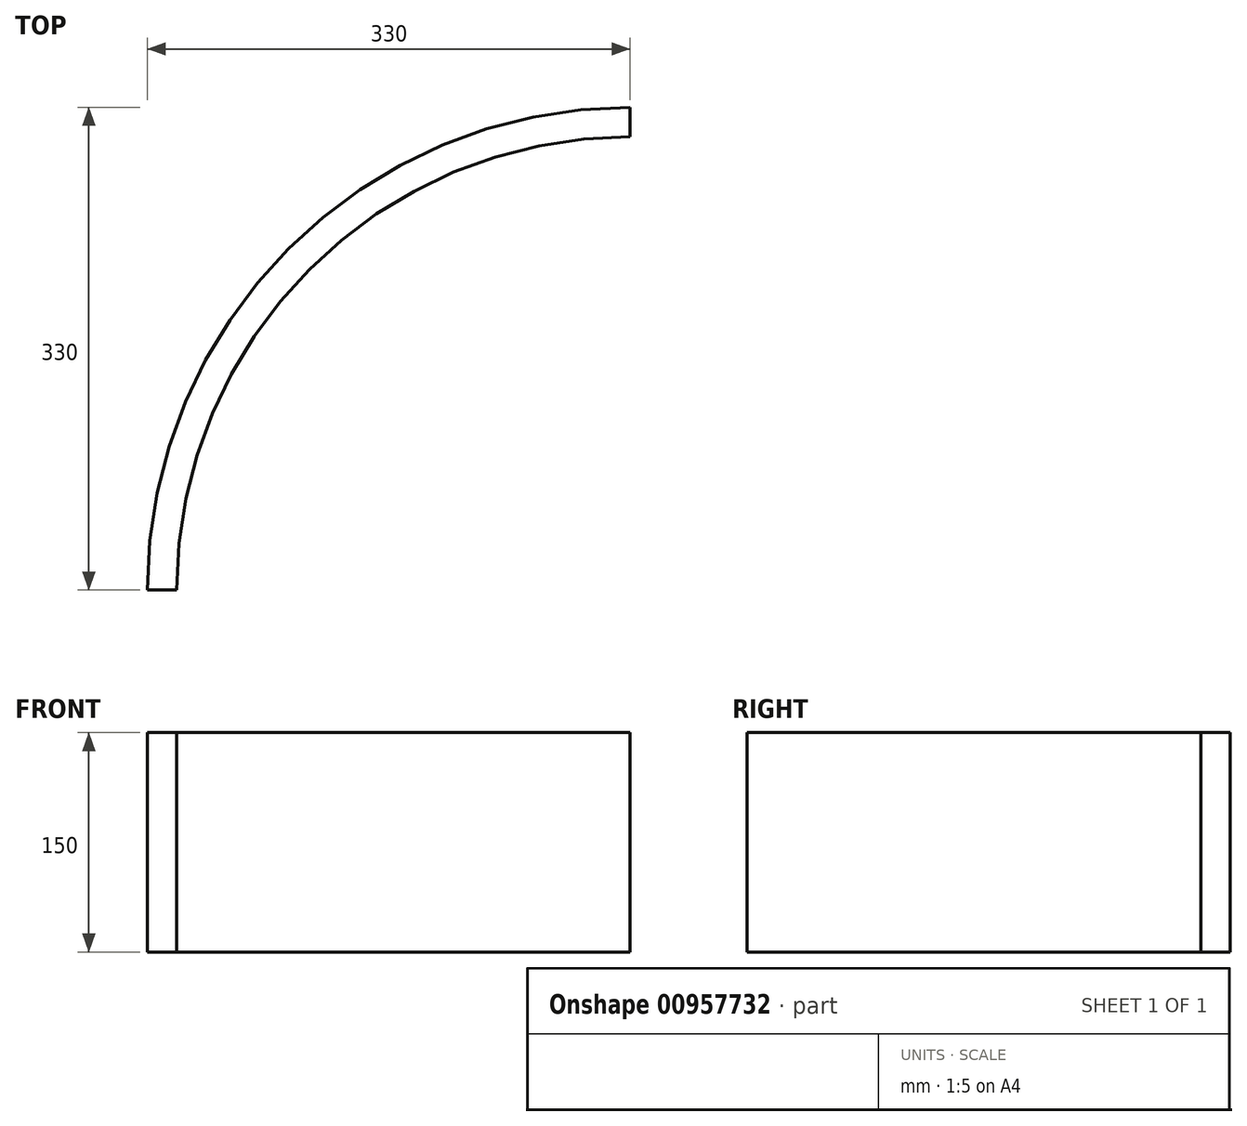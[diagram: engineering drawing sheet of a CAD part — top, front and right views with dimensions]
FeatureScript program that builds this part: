
annotation { "Feature Type Name" : "Feature", "Feature Type Description" : "" }
export const myFeature = defineFeature(function(context is Context, id is Id, definition is map)
    precondition{}
    {
        {
            var Q0;
            Q0=qCreatedBy(makeId("Top.planeOp"),FACE);
            var sketch = newSketch(context, id + "F0", { "sketchPlane" : qUnion([Q0])});
            skArc(sketch, "E0", {"start": v(-310, 0) * mm, "mid": v(-219.2, 219.2) * mm, "end": v(0, 310) * mm});
            skArc(sketch, "E1", {"start": v(-330, 0) * mm, "mid": v(-233.35, 233.35) * mm, "end": v(0, 330) * mm});
            skLineSegment(sketch, "E2", {"start": v(0, 330) * mm, "end": v(0, 310) * mm});
            skLineSegment(sketch, "E3", {"start": v(-330, 0) * mm, "end": v(-310, 0) * mm});
            skSolve(sketch);
        }
        {
            var Q0;
            Q0 = qSketchRegion(id + "F0", true);
            extrude(context, id + "F1", {"entities" : qUnion([Q0]), "depth" : 150 * mm, "offsetDistance" : 25 * mm});
        }
    });
